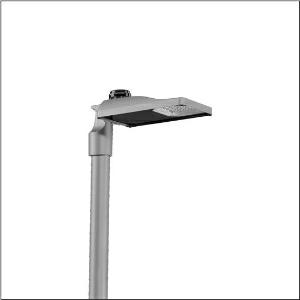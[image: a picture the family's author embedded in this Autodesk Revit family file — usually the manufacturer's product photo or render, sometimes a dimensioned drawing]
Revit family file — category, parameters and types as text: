
# Revit family: streetlight_sl_31_micro___p1_0a_5xh5a75n08ca_0299
name_source: partatom
category: Lighting Fixtures
units: mm (PartAtom-declared; Revit-internal decimal feet)

## family parameters
Cut with Voids When Loaded = No
Host = Face
Light Source = No
Part Type = Normal
Room Calculation Point = No
Round Connector Dimension = Use Diameter
Shared = No

## types (1)
- --- (1 x LED, 1080 lm, 10.3 W, 2200K)
    Apparent Load = 10 VA
    CIE Flux Codes = 23 55 94 100 100
    Color Rendering = 70
    Color Temperature = 2200K
    Default Elevation = 1800 mm
    Description = Streetlight SL 31 micro NEMA (7pin), Desk-Remote mast luminaire for post-top, side-entry; light control with lens of PMMA; light distribution: P1.0a, direct asymmetric distribution, for standard-compliant lighting for roads and squares; LED: luminous flux: 1.080lm, light colour: 722, colour temperature: 2200K; luminous efficacy: 104,9lm/W; control: pre-setting: linear dimming characteristic, flexible luminous flux parameterisation, time-dependent luminous flux control, constant luminous flux control, intelligent temperature release in ECG and LED module, overheat protection; luminaire housing, of diecast aluminium, SITECO metallic grey (DB 702S), corrosivity category C5 high according to DIN EN ISO 12944; cover of toughened safety glass, transparent, opened without tools; mast flange of diecast aluminium, SITECO metallic grey (DB 702S), spigot size: 76/60mm, mast flange included unmounted; cable length: 5,5m, connection cable pre-assembled; mains connection: 220..240V, AC, 50/60Hz; power consumption (at start of service life): 10,3W / (at end of service life): 10,6W / (with reduced operation 50%): 5,3W; protection rating (complete): IP66; insulation class (complete): insulation class I (protective earthing); impact resistance: IK10; certification: CE, ENEC, ENEC+, VDE, UKCA; permissible operating ambient temperature for outdoor applications: -40..+50°C; packaging unit: 1 piece

Light Distribution: P1.0a
    Height = 76 mm
    Lamp = 1 x LED
    Lamp Light Flux = 1080 lm
    Lamp Power = 10.3 W
    Lamp count = 1
    Length = 467 mm
    Luminous efficacy = 105 lm/W
    Manufacturer = Siteco
    ModVariant = No
    Model = 5XH5A75N08CA
    Mounting Place = Pole
    Mounting Type = Pole top
    Number of Poles = 1
    OnlyDefault = Yes
    Power Factor = 1
    Product Name = Streetlight SL 31 micro | P1.0a
    Product group = mast luminaire | pylon top
    ProductGroupID = 6100
    Protection Class = Protection class I
    Protection Degree = IP 66
    RLX_Detail_Level = 1
    RLX_Emergency_Light_Flux = 0 lm
    RLX_Emergency_Type = 0
    RLX_Emergency_Type_DB = No
    RlxData = <blob elided: 22617 chars, md5=1d58cff0>
    Socket = socket
    Standby Power = 0 W
    System Light Flux = 1080 lm
    System Power = 10 W
    Type Comments = factory setting: luminous flux: 100 % | dim-lin: 254 | 386 mA
    Type Image = l_1300305.jpg
    URL = http://relux.com
    VarID = @adj_010539
    Voltage = 0 V
    Weight = 0.00 kg
    Width = 265 mm

## geometry (parser evidence)
native form markers: Blend x4, Sweep x13
no freeform markers — native parametric forms only
